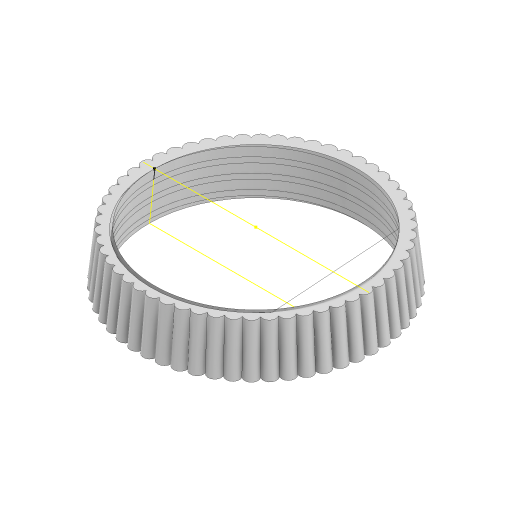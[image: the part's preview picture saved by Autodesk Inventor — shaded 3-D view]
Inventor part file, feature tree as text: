
AUTODESK INVENTOR PART (.ipt)
format: ipt  version: 2023 (Build 270158000, 158)  size: 464,896 bytes
history: native  units: mm
features: sketch x5, draft x2, helix x2, extrude x1, sweep x1, pattern_circular x1
ambient origin geometry x8: Origin, YZ Plane, XZ Plane, XY Plane, X Axis, Y Axis, Z Axis, Center Point
bodies: Solid1 (feature_tree)
feature tree (12):
  extrude  "Extrusion1"  Depth=6.52mm TaperAngle=0.0deg
  draft  "FaceDraft1"
  sketch  "Sketch2"  dims[d7=2.0mm d8=9.0mm d9=10.0mm d10=1.047198mm d11=90.0deg d12=90.0deg d13=0.0mm d14=0.0mm d15=2.0mm d16=3.0mm d17=10.0mm d18=-1.047198mm d19=90.0deg d20=90.0deg d21=0.0mm d22=0.0mm d23=1.5mm d91=1.047198mm]
  sketch  "Sketch4"  dims[d93=1.75mm d95=0.0mm d96=0.0mm d97=540.0mm d98=360.0deg]
  helix  "Coil1"  [1 undecoded]
  helix  "Coil2"  [1 undecoded]
  draft  "FaceDraft2"
  sweep  "Sweep1"
  pattern_circular  "Circular Pattern3"  Count=54 Angle=360.0deg
  sketch  "Sketch1"  dims[d0=26.5mm d2=6.52mm d3=0.0mm d4=1.047198mm]
  sketch  "Sketch9"
  sketch  "Sketch10"
note: 2 required parameter values undecoded (feature->parameter linkage not recoverable at this tier; creation-order binding heuristic only, values carry confidence <= 0.55)
